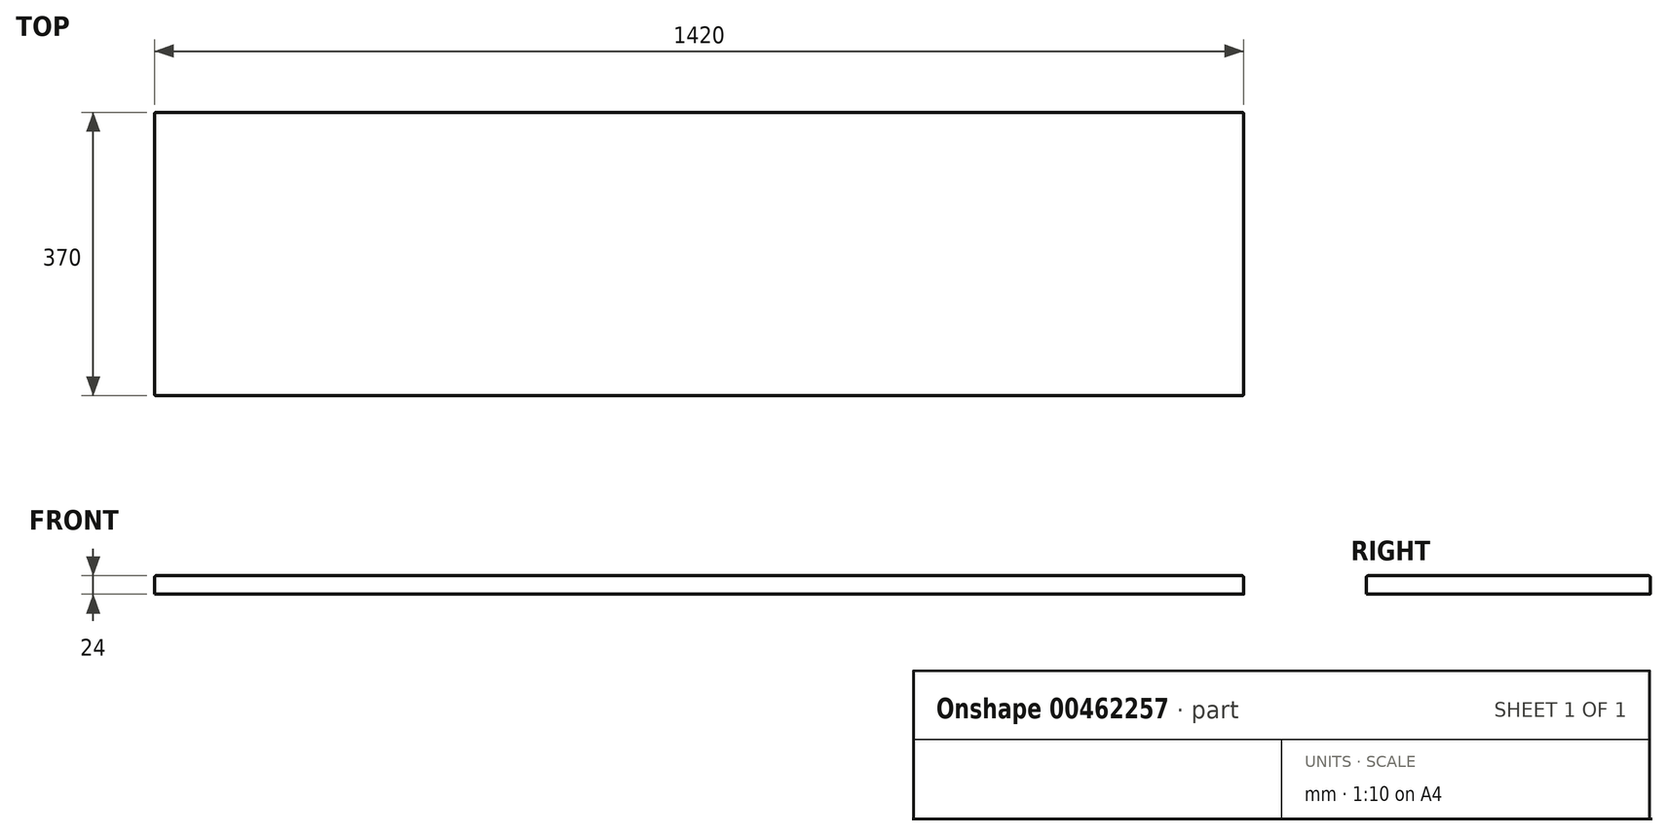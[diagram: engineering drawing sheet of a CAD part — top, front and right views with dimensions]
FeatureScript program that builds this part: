
annotation { "Feature Type Name" : "Feature", "Feature Type Description" : "" }
export const myFeature = defineFeature(function(context is Context, id is Id, definition is map)
    precondition{}
    {
        {
            var Q0;
            Q0=qCreatedBy(makeId("Top.planeOp"),FACE);
            var sketch = newSketch(context, id + "F0", { "sketchPlane" : qUnion([Q0])});
            skLineSegment(sketch, "E0.bottom", {"start": v(730.33, -185) * mm, "end": v(-689.67, -185) * mm});
            skLineSegment(sketch, "E0.top", {"start": v(730.33, 185) * mm, "end": v(-689.67, 185) * mm});
            skLineSegment(sketch, "E0.left", {"start": v(730.33, -185) * mm, "end": v(730.33, 185) * mm});
            skLineSegment(sketch, "E0.right", {"start": v(-689.67, -185) * mm, "end": v(-689.67, 185) * mm});
            skPoint(sketch, "E0.middle", {"position": v(20.33, 0) * mm});
            skSolve(sketch);
        }
        {
            var Q0;
            Q0=makeQuery(id+"F0.imprint","IMPRINT",FACE,{"disambiguationData":[TD([[makeQuery(id+"F0.imprint","IMPRINT",EDGE,{"derivedFrom":sQuery(id+"F0.wireOp",EDGE,"E0.bottom")}),-1.0]])]});
            extrude(context, id + "F1", {"entities" : qUnion([Q0]), "depth" : 24 * mm});
        }
        {
            var Q0;
            Q0=makeQuery(id+"F1.opExtrude","CAP_EDGE",EDGE,{"disambiguationData":[OSD([sQuery(id+"F0.wireOp",EDGE,"E0.bottom")])],"isStart":false});
            fillet(context, id + "F2", {"entities" : qUnion([Q0]), "radius" : 2 * mm, "tangentPropagation" : true, "allowEdgeOverflow" : false});
        }
        {
            var Q0;
            Q0=makeQuery(id+"F1.opExtrude","CAP_EDGE",EDGE,{"disambiguationData":[OSD([sQuery(id+"F0.wireOp",EDGE,"E0.right")])],"isStart":false});
            var Q1;
            Q1=makeQuery(id+"F1.opExtrude","CAP_EDGE",EDGE,{"disambiguationData":[OSD([sQuery(id+"F0.wireOp",EDGE,"E0.left")])],"isStart":false});
            var Q2;
            Q2=makeQuery(id+"F1.opExtrude","CAP_EDGE",EDGE,{"disambiguationData":[OSD([sQuery(id+"F0.wireOp",EDGE,"E0.top")])],"isStart":false});
            fillet(context, id + "F3", {"entities" : qUnion([Q0, Q1, Q2]), "radius" : 2 * mm, "tangentPropagation" : true, "allowEdgeOverflow" : false});
        }
        {
            var Q0;
            Q0=makeQuery(id+"F1.opExtrude","SWEPT_EDGE",EDGE,{"disambiguationData":[OSD([sQuery(id+"F0.wireOp",EDGE,"E0.top"),sQuery(id+"F0.wireOp",EDGE,"E0.left")])]});
            fillet(context, id + "F4", {"entities" : qUnion([Q0]), "radius" : 2 * mm, "tangentPropagation" : true, "allowEdgeOverflow" : false});
        }
        {
            var Q0;
            Q0=makeQuery(id+"F1.opExtrude","SWEPT_EDGE",EDGE,{"disambiguationData":[OSD([sQuery(id+"F0.wireOp",EDGE,"E0.top"),sQuery(id+"F0.wireOp",EDGE,"E0.right")])]});
            fillet(context, id + "F5", {"entities" : qUnion([Q0]), "radius" : 2 * mm, "tangentPropagation" : true, "allowEdgeOverflow" : false});
        }
    });
